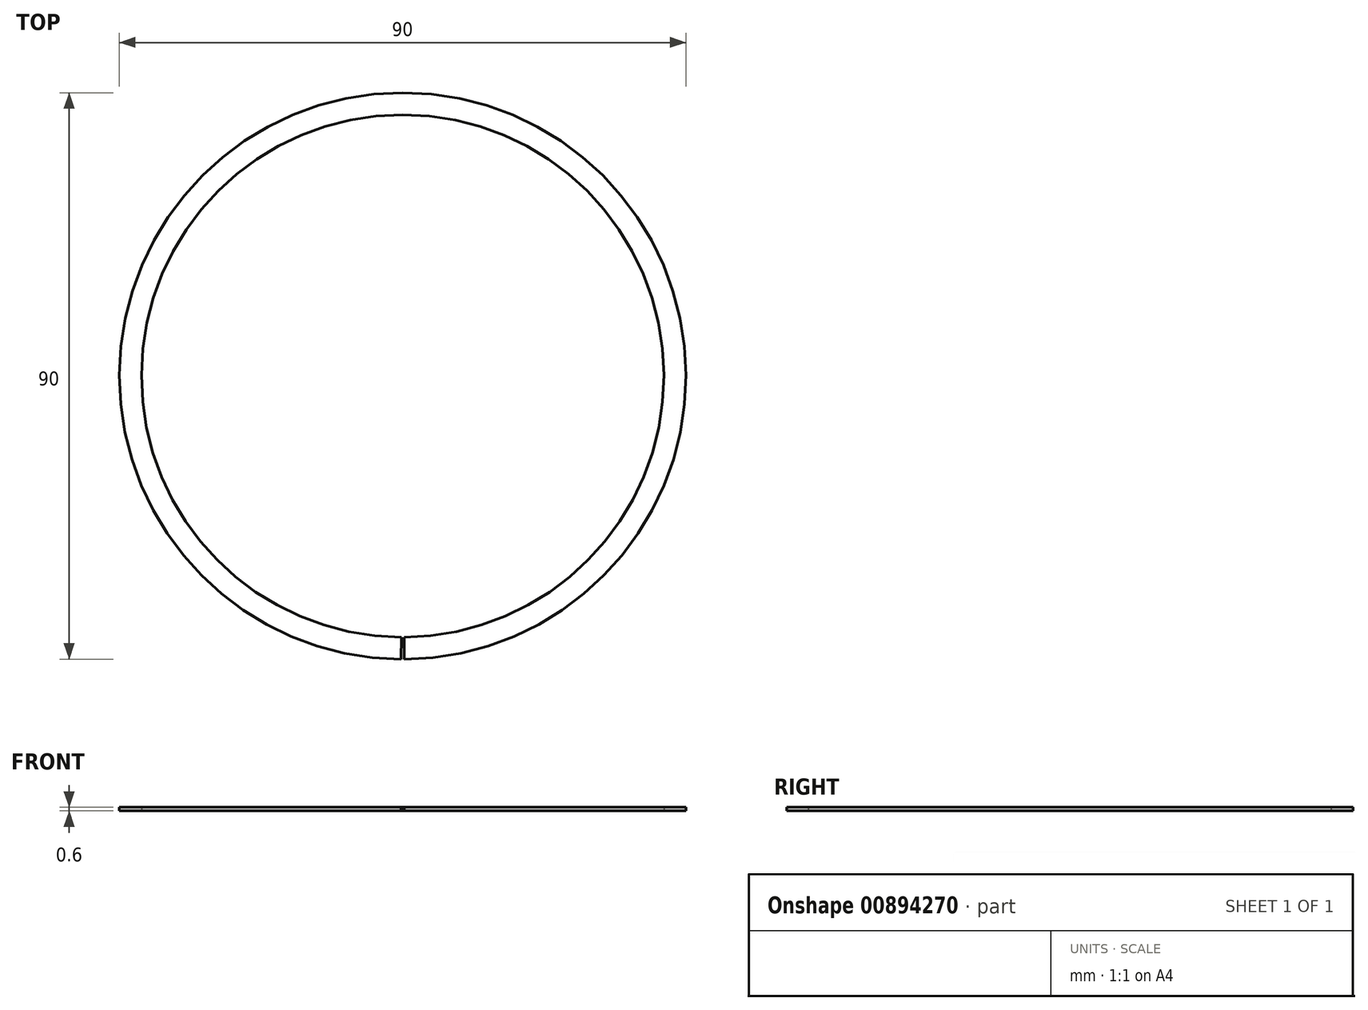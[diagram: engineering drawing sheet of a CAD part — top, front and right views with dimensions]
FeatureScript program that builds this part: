
annotation { "Feature Type Name" : "Feature", "Feature Type Description" : "" }
export const myFeature = defineFeature(function(context is Context, id is Id, definition is map)
    precondition{}
    {
        {
            var Q0;
            Q0=qCreatedBy(makeId("Right.planeOp"),FACE);
            var sketch = newSketch(context, id + "F0", { "sketchPlane" : qUnion([Q0])});
            skLineSegment(sketch, "E0", {"start": v(0, 0) * mm, "end": v(41.5, 0) * mm, "construction": true});
            skLineSegment(sketch, "E1.bottom", {"start": v(41.5, 0) * mm, "end": v(45, 0) * mm});
            skLineSegment(sketch, "E1.top", {"start": v(41.5, 0.6) * mm, "end": v(45, 0.6) * mm});
            skLineSegment(sketch, "E1.left", {"start": v(41.5, 0) * mm, "end": v(41.5, 0.6) * mm});
            skLineSegment(sketch, "E1.right", {"start": v(45, 0) * mm, "end": v(45, 0.6) * mm});
            skLineSegment(sketch, "E2", {"start": v(0, 0) * mm, "end": v(0, 20) * mm, "construction": true});
            skSolve(sketch);
        }
        {
            var Q0;
            Q0=makeQuery(id+"F0.imprint","IMPRINT",FACE,{"disambiguationData":[TD([[makeQuery(id+"F0.imprint","IMPRINT",EDGE,{"derivedFrom":sQuery(id+"F0.wireOp",EDGE,"E1.bottom")}),1.0]])]});
            var Q1;
            Q1=sQuery(id+"F0.wireOp",EDGE,"E2");
            revolve(context, id + "F1", {"surfaceOperationType" : NewSurfaceOperationType.NEW, "entities" : qUnion([Q0]), "axis" : qUnion([Q1]), "revolveType" : RevolveType.TWO_DIRECTIONS, "angle" : 179.7 * degree, "angleBack" : 180.3 * degree});
        }
    });
